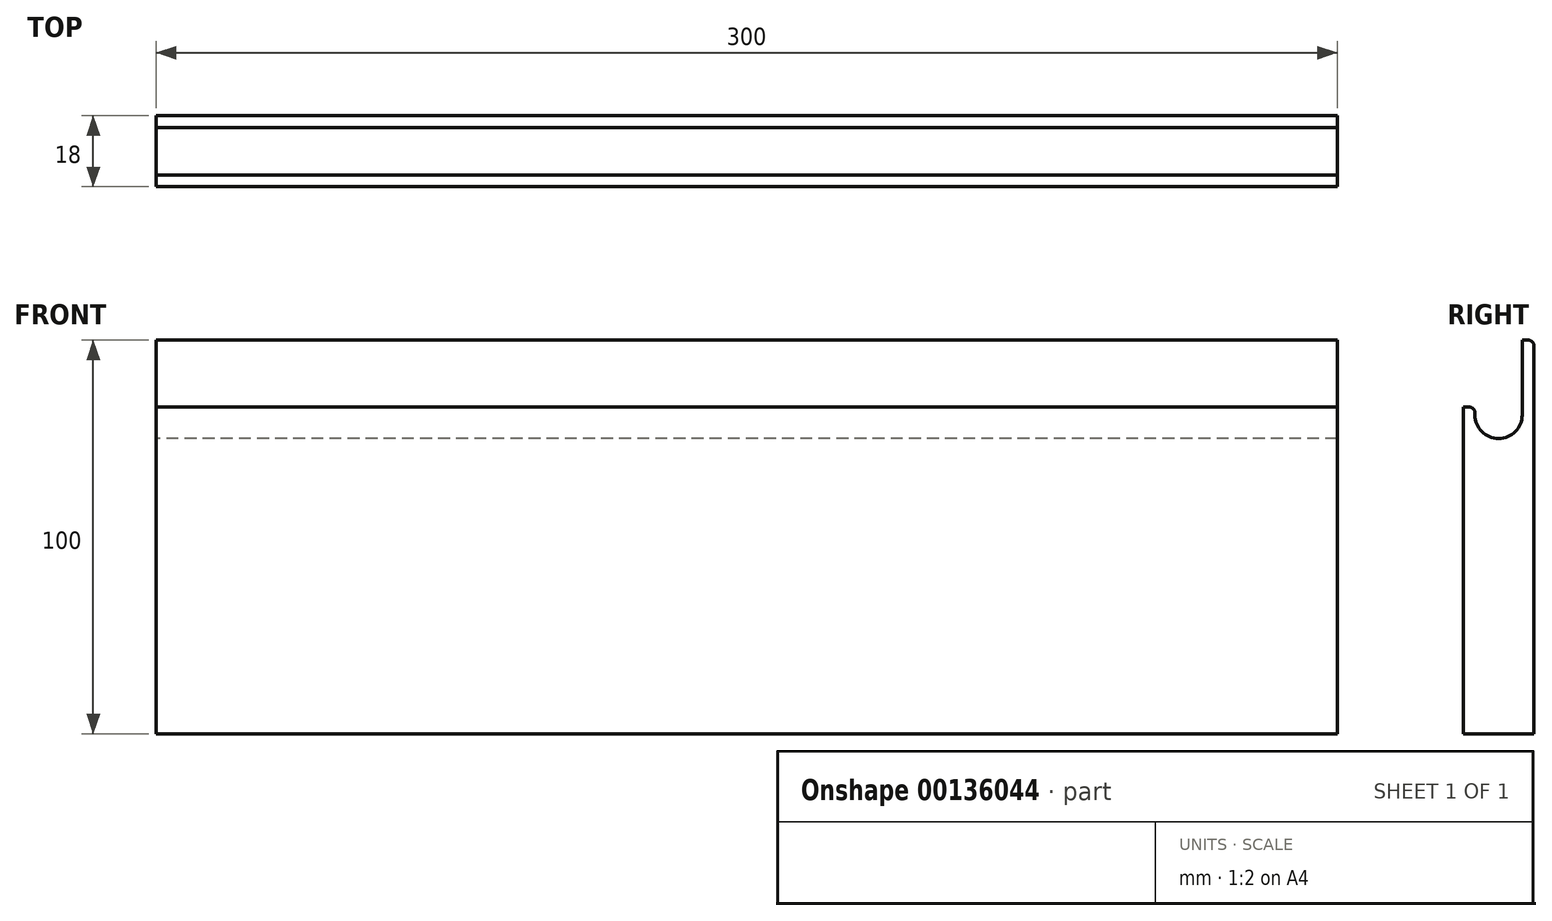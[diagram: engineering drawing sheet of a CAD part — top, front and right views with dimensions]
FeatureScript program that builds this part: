
annotation { "Feature Type Name" : "Feature", "Feature Type Description" : "" }
export const myFeature = defineFeature(function(context is Context, id is Id, definition is map)
    precondition{}
    {
        {
            var Q0;
            Q0=qCreatedBy(makeId("Front.planeOp"),FACE);
            var sketch = newSketch(context, id + "F0", { "sketchPlane" : qUnion([Q0])});
            skLineSegment(sketch, "E0.bottom", {"start": v(-153.72, -55.78) * mm, "end": v(146.28, -55.78) * mm});
            skLineSegment(sketch, "E0.top", {"start": v(-153.72, -155.78) * mm, "end": v(146.28, -155.78) * mm});
            skLineSegment(sketch, "E0.left", {"start": v(-153.72, -55.78) * mm, "end": v(-153.72, -155.78) * mm});
            skLineSegment(sketch, "E0.right", {"start": v(146.28, -55.78) * mm, "end": v(146.28, -155.78) * mm});
            skSolve(sketch);
        }
        {
            var Q0;
            Q0=makeQuery(id+"F0.imprint","IMPRINT",FACE,{"disambiguationData":[TD([[makeQuery(id+"F0.imprint","IMPRINT",EDGE,{"derivedFrom":sQuery(id+"F0.wireOp",EDGE,"E0.bottom")}),-1.0]])]});
            extrude(context, id + "F1", {"entities" : qUnion([Q0]), "endBound" : BoundingType.SYMMETRIC, "depth" : 18 * mm});
        }
        {
            var Q0;
            Q0=makeQuery(id+"F1.opExtrude","SWEPT_FACE",FACE,{"disambiguationData":[OSD([sQuery(id+"F0.wireOp",EDGE,"E0.right")])]});
            var sketch = newSketch(context, id + "F2", { "sketchPlane" : qUnion([Q0])});
            skLineSegment(sketch, "E1", {"start": v(-9, -55.78) * mm, "end": v(6, -55.78) * mm});
            skLineSegment(sketch, "E2", {"start": v(6, -55.78) * mm, "end": v(6, -80.78) * mm});
            skLineSegment(sketch, "E3", {"start": v(6, -80.78) * mm, "end": v(-6, -80.78) * mm});
            skLineSegment(sketch, "E4", {"start": v(-6, -80.78) * mm, "end": v(-6, -72.78) * mm});
            skLineSegment(sketch, "E5", {"start": v(-6, -72.78) * mm, "end": v(-9, -72.78) * mm});
            skLineSegment(sketch, "E6", {"start": v(-9, -72.78) * mm, "end": v(-9, -55.78) * mm});
            skSolve(sketch);
        }
        {
            var Q0;
            Q0=makeQuery(id+"F2.imprint","IMPRINT",FACE,{"disambiguationData":[TD([[makeQuery(id+"F2.imprint","IMPRINT",EDGE,{"derivedFrom":sQuery(id+"F2.wireOp",EDGE,"E1")}),-1.0]])]});
            extrude(context, id + "F3", {"entities" : qUnion([Q0]), "operationType" : NewBodyOperationType.REMOVE, "endBound" : BoundingType.THROUGH_ALL, "oppositeDirection" : true, "depth" : 25 * mm});
        }
        {
            var Q0;
            Q0=makeQuery(id+"F3.boolean.opBoolean","COPY",EDGE,{"derivedFrom":makeQuery(id+"F3.opExtrude","SWEPT_EDGE",EDGE,{"disambiguationData":[OSD([sQuery(id+"F0.wireOp",EDGE,"E0.bottom"),sQuery(id+"F0.wireOp",EDGE,"E0.right"),sQuery(id+"F2.wireOp",EDGE,"E1"),sQuery(id+"F2.wireOp",EDGE,"E2")])]})});
            var Q1;
            Q1=makeQuery(id+"F1.opExtrude","CAP_EDGE",EDGE,{"disambiguationData":[OSD([sQuery(id+"F0.wireOp",EDGE,"E0.bottom")])],"isStart":true});
            var Q2;
            Q2=makeQuery(id+"F3.boolean.opBoolean","COPY",EDGE,{"derivedFrom":makeQuery(id+"F3.opExtrude","SWEPT_EDGE",EDGE,{"disambiguationData":[OSD([sQuery(id+"F0.wireOp",EDGE,"E0.right"),sQuery(id+"F2.wireOp",EDGE,"E5"),sQuery(id+"F2.wireOp",EDGE,"E6")])]})});
            var Q3;
            Q3=makeQuery(id+"F3.boolean.opBoolean","COPY",EDGE,{"derivedFrom":makeQuery(id+"F3.opExtrude","SWEPT_EDGE",EDGE,{"disambiguationData":[OSD([sQuery(id+"F2.wireOp",EDGE,"E4"),sQuery(id+"F2.wireOp",EDGE,"E5")])]})});
            fillet(context, id + "F4", {"entities" : qUnion([Q0, Q1, Q2, Q3]), "radius" : 1.5 * mm, "tangentPropagation" : true, "allowEdgeOverflow" : false});
        }
        {
            var Q0;
            Q0=makeQuery(id+"F3.boolean.opBoolean","COPY",EDGE,{"derivedFrom":makeQuery(id+"F3.opExtrude","SWEPT_EDGE",EDGE,{"disambiguationData":[OSD([sQuery(id+"F2.wireOp",EDGE,"E2"),sQuery(id+"F2.wireOp",EDGE,"E3")])]})});
            var Q1;
            Q1=makeQuery(id+"F3.boolean.opBoolean","COPY",EDGE,{"derivedFrom":makeQuery(id+"F3.opExtrude","SWEPT_EDGE",EDGE,{"disambiguationData":[OSD([sQuery(id+"F2.wireOp",EDGE,"E3"),sQuery(id+"F2.wireOp",EDGE,"E4")])]})});
            fillet(context, id + "F5", {"entities" : qUnion([Q0, Q1]), "radius" : 6 * mm, "tangentPropagation" : true, "allowEdgeOverflow" : false});
        }
    });
